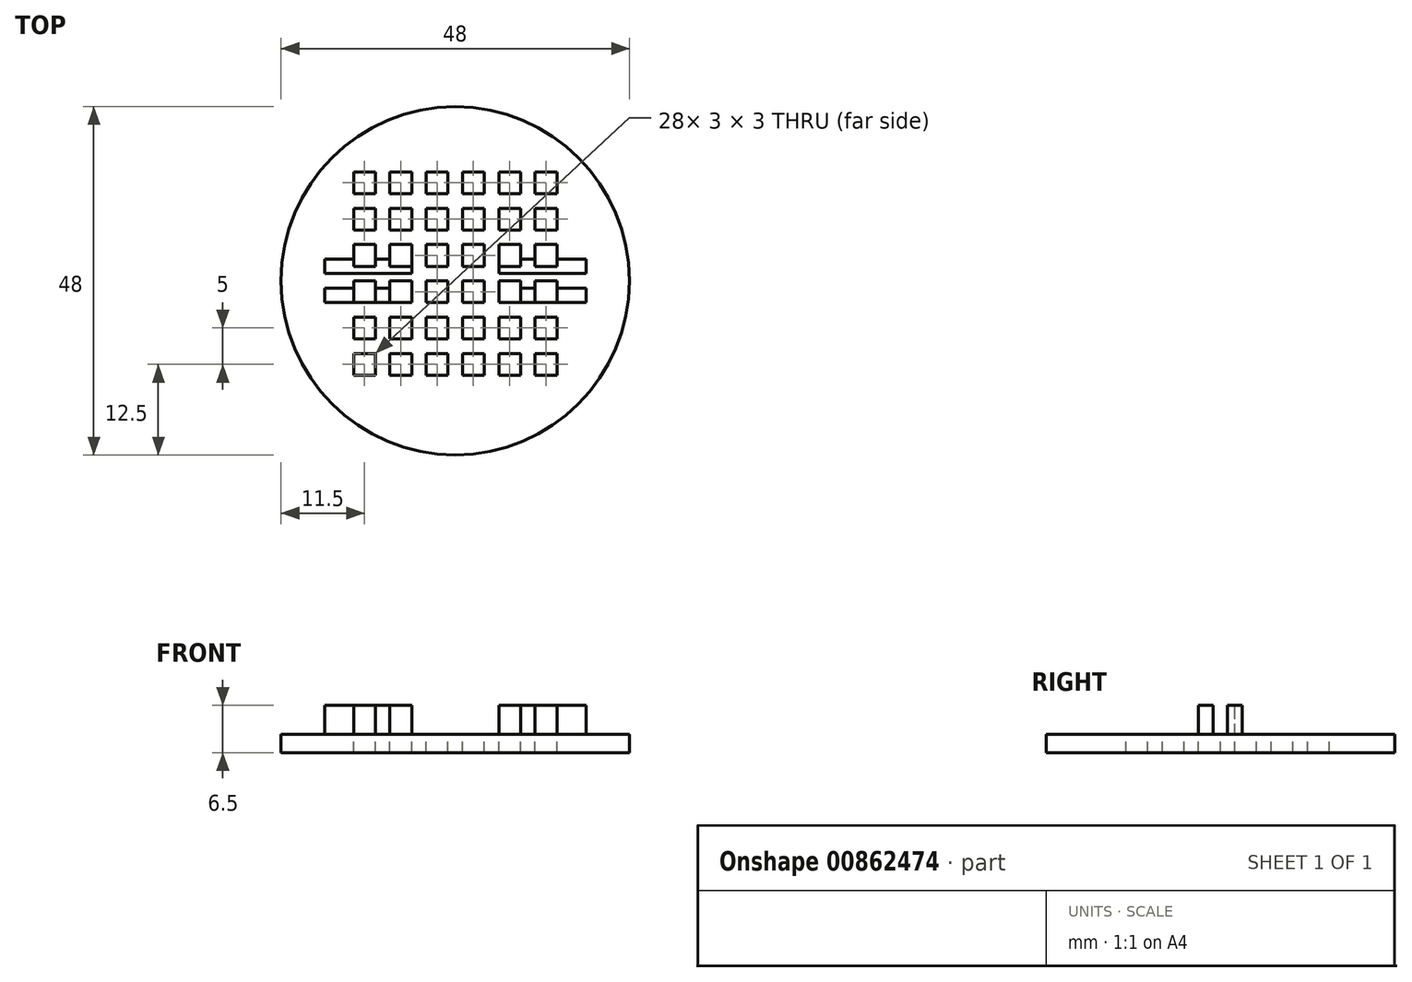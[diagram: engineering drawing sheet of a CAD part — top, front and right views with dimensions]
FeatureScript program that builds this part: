
annotation { "Feature Type Name" : "Feature", "Feature Type Description" : "" }
export const myFeature = defineFeature(function(context is Context, id is Id, definition is map)
    precondition{}
    {
        {
            var Q0;
            Q0=qCreatedBy(makeId("Top.planeOp"),FACE);
            var sketch = newSketch(context, id + "F0", { "sketchPlane" : qUnion([Q0])});
            skCircle(sketch, "E0", {"center": v(0, 0) * mm, "radius": 24 * mm});
            skSolve(sketch);
        }
        {
            var Q0;
            Q0 = qSketchRegion(id + "F0", true);
            extrude(context, id + "F1", {"entities" : qUnion([Q0]), "depth" : 2.5 * mm, "offsetDistance" : 25 * mm});
        }
        {
            var Q0;
            Q0=makeQuery(id+"F1.opExtrude","CAP_FACE",FACE,{"disambiguationData":[OSD([sQuery(id+"F0.wireOp",EDGE,"E0")])],"isStart":false});
            var sketch = newSketch(context, id + "F2", { "sketchPlane" : qUnion([Q0])});
            skCircle(sketch, "E1", {"center": v(-0.3, 0) * mm, "radius": 22 * mm});
            skSolve(sketch);
        }
        {
            var Q0;
            Q0=makeQuery(id+"F2.imprint","IMPRINT",FACE,{"disambiguationData":[TD([[makeQuery(id+"F2.imprint","IMPRINT",EDGE,{"derivedFrom":sQuery(id+"F2.wireOp",EDGE,"E1")}),1.0]])]});
            var sketch = newSketch(context, id + "F3", { "sketchPlane" : qUnion([Q0])});
            skLineSegment(sketch, "E2", {"start": v(-22.27, 1) * mm, "end": v(21.68, 1) * mm});
            skLineSegment(sketch, "E3", {"start": v(21.68, -1) * mm, "end": v(-22.27, -1) * mm});
            skLineSegment(sketch, "E4", {"start": v(6, -1) * mm, "end": v(6, 1) * mm});
            skLineSegment(sketch, "E5", {"start": v(-6, -1) * mm, "end": v(-6, 1) * mm});
            skSolve(sketch);
        }
        {
            var Q0;
            Q0=makeQuery(id+"F2.imprint","IMPRINT",FACE,{"disambiguationData":[TD([[makeQuery(id+"F2.imprint","IMPRINT",EDGE,{"derivedFrom":sQuery(id+"F2.wireOp",EDGE,"E1")}),1.0]])]});
            var sketch = newSketch(context, id + "F4", { "sketchPlane" : qUnion([Q0])});
            skLineSegment(sketch, "E6.bottom", {"start": v(18, -3) * mm, "end": v(6, -3) * mm});
            skLineSegment(sketch, "E6.top", {"start": v(18, -1) * mm, "end": v(6, -1) * mm});
            skLineSegment(sketch, "E6.left", {"start": v(18, -3) * mm, "end": v(18, -1) * mm});
            skLineSegment(sketch, "E6.right", {"start": v(6, -3) * mm, "end": v(6, -1) * mm});
            skLineSegment(sketch, "E7.bottom", {"start": v(6, 1) * mm, "end": v(18, 1) * mm});
            skLineSegment(sketch, "E7.top", {"start": v(6, 3) * mm, "end": v(18, 3) * mm});
            skLineSegment(sketch, "E7.left", {"start": v(6, 1) * mm, "end": v(6, 3) * mm});
            skLineSegment(sketch, "E7.right", {"start": v(18, 1) * mm, "end": v(18, 3) * mm});
            skLineSegment(sketch, "E8.bottom", {"start": v(-18, -1) * mm, "end": v(-6, -1) * mm});
            skLineSegment(sketch, "E8.top", {"start": v(-18, -3) * mm, "end": v(-6, -3) * mm});
            skLineSegment(sketch, "E8.left", {"start": v(-18, -1) * mm, "end": v(-18, -3) * mm});
            skLineSegment(sketch, "E8.right", {"start": v(-6, -1) * mm, "end": v(-6, -3) * mm});
            skLineSegment(sketch, "E9.bottom", {"start": v(-18, 1) * mm, "end": v(-6, 1) * mm});
            skLineSegment(sketch, "E9.top", {"start": v(-18, 3) * mm, "end": v(-6, 3) * mm});
            skLineSegment(sketch, "E9.left", {"start": v(-18, 1) * mm, "end": v(-18, 3) * mm});
            skLineSegment(sketch, "E9.right", {"start": v(-6, 1) * mm, "end": v(-6, 3) * mm});
            skSolve(sketch);
        }
        {
            var Q0;
            Q0 = qSketchRegion(id + "F4", true);
            extrude(context, id + "F5", {"entities" : qUnion([Q0]), "operationType" : NewBodyOperationType.ADD, "depth" : 4 * mm, "offsetDistance" : 25 * mm});
        }
        {
            var Q0;
            Q0=makeQuery(id+"F2.imprint","IMPRINT",FACE,{"disambiguationData":[TD([[makeQuery(id+"F2.imprint","IMPRINT",EDGE,{"derivedFrom":sQuery(id+"F2.wireOp",EDGE,"E1")}),1.0]])]});
            var sketch = newSketch(context, id + "F6", { "sketchPlane" : qUnion([Q0])});
            skLineSegment(sketch, "E10.bottom", {"start": v(11, -10) * mm, "end": v(14, -10) * mm});
            skLineSegment(sketch, "E10.top", {"start": v(11, -13) * mm, "end": v(14, -13) * mm});
            skLineSegment(sketch, "E10.left", {"start": v(11, -10) * mm, "end": v(11, -13) * mm});
            skLineSegment(sketch, "E10.right", {"start": v(14, -10) * mm, "end": v(14, -13) * mm});
            skLineSegment(sketch, "E11.0.1.0", {"start": v(11, -5) * mm, "end": v(14, -5) * mm});
            skLineSegment(sketch, "E11.0.1.1", {"start": v(11, -5) * mm, "end": v(11, -8) * mm});
            skLineSegment(sketch, "E11.0.1.2", {"start": v(11, -8) * mm, "end": v(14, -8) * mm});
            skLineSegment(sketch, "E11.0.1.3", {"start": v(14, -5) * mm, "end": v(14, -8) * mm});
            skLineSegment(sketch, "E11.0.2.0", {"start": v(11, 0) * mm, "end": v(14, 0) * mm});
            skLineSegment(sketch, "E11.0.2.1", {"start": v(11, 0) * mm, "end": v(11, -3) * mm});
            skLineSegment(sketch, "E11.0.2.2", {"start": v(11, -3) * mm, "end": v(14, -3) * mm});
            skLineSegment(sketch, "E11.0.2.3", {"start": v(14, 0) * mm, "end": v(14, -3) * mm});
            skLineSegment(sketch, "E11.0.3.0", {"start": v(11, 5) * mm, "end": v(14, 5) * mm});
            skLineSegment(sketch, "E11.0.3.1", {"start": v(11, 5) * mm, "end": v(11, 2) * mm});
            skLineSegment(sketch, "E11.0.3.2", {"start": v(11, 2) * mm, "end": v(14, 2) * mm});
            skLineSegment(sketch, "E11.0.3.3", {"start": v(14, 5) * mm, "end": v(14, 2) * mm});
            skLineSegment(sketch, "E11.0.4.0", {"start": v(11, 10) * mm, "end": v(14, 10) * mm});
            skLineSegment(sketch, "E11.0.4.1", {"start": v(11, 10) * mm, "end": v(11, 7) * mm});
            skLineSegment(sketch, "E11.0.4.2", {"start": v(11, 7) * mm, "end": v(14, 7) * mm});
            skLineSegment(sketch, "E11.0.4.3", {"start": v(14, 10) * mm, "end": v(14, 7) * mm});
            skLineSegment(sketch, "E11.0.5.0", {"start": v(11, 15) * mm, "end": v(14, 15) * mm});
            skLineSegment(sketch, "E11.0.5.1", {"start": v(11, 15) * mm, "end": v(11, 12) * mm});
            skLineSegment(sketch, "E11.0.5.2", {"start": v(11, 12) * mm, "end": v(14, 12) * mm});
            skLineSegment(sketch, "E11.0.5.3", {"start": v(14, 15) * mm, "end": v(14, 12) * mm});
            skLineSegment(sketch, "E11.1.0.0", {"start": v(6, -10) * mm, "end": v(9, -10) * mm});
            skLineSegment(sketch, "E11.1.0.1", {"start": v(6, -10) * mm, "end": v(6, -13) * mm});
            skLineSegment(sketch, "E11.1.0.2", {"start": v(6, -13) * mm, "end": v(9, -13) * mm});
            skLineSegment(sketch, "E11.1.0.3", {"start": v(9, -10) * mm, "end": v(9, -13) * mm});
            skLineSegment(sketch, "E11.1.1.0", {"start": v(6, -5) * mm, "end": v(9, -5) * mm});
            skLineSegment(sketch, "E11.1.1.1", {"start": v(6, -5) * mm, "end": v(6, -8) * mm});
            skLineSegment(sketch, "E11.1.1.2", {"start": v(6, -8) * mm, "end": v(9, -8) * mm});
            skLineSegment(sketch, "E11.1.1.3", {"start": v(9, -5) * mm, "end": v(9, -8) * mm});
            skLineSegment(sketch, "E11.1.2.0", {"start": v(6, 0) * mm, "end": v(9, 0) * mm});
            skLineSegment(sketch, "E11.1.2.1", {"start": v(6, 0) * mm, "end": v(6, -3) * mm});
            skLineSegment(sketch, "E11.1.2.2", {"start": v(6, -3) * mm, "end": v(9, -3) * mm});
            skLineSegment(sketch, "E11.1.2.3", {"start": v(9, 0) * mm, "end": v(9, -3) * mm});
            skLineSegment(sketch, "E11.1.3.0", {"start": v(6, 5) * mm, "end": v(9, 5) * mm});
            skLineSegment(sketch, "E11.1.3.1", {"start": v(6, 5) * mm, "end": v(6, 2) * mm});
            skLineSegment(sketch, "E11.1.3.2", {"start": v(6, 2) * mm, "end": v(9, 2) * mm});
            skLineSegment(sketch, "E11.1.3.3", {"start": v(9, 5) * mm, "end": v(9, 2) * mm});
            skLineSegment(sketch, "E11.1.4.0", {"start": v(6, 10) * mm, "end": v(9, 10) * mm});
            skLineSegment(sketch, "E11.1.4.1", {"start": v(6, 10) * mm, "end": v(6, 7) * mm});
            skLineSegment(sketch, "E11.1.4.2", {"start": v(6, 7) * mm, "end": v(9, 7) * mm});
            skLineSegment(sketch, "E11.1.4.3", {"start": v(9, 10) * mm, "end": v(9, 7) * mm});
            skLineSegment(sketch, "E11.1.5.0", {"start": v(6, 15) * mm, "end": v(9, 15) * mm});
            skLineSegment(sketch, "E11.1.5.1", {"start": v(6, 15) * mm, "end": v(6, 12) * mm});
            skLineSegment(sketch, "E11.1.5.2", {"start": v(6, 12) * mm, "end": v(9, 12) * mm});
            skLineSegment(sketch, "E11.1.5.3", {"start": v(9, 15) * mm, "end": v(9, 12) * mm});
            skLineSegment(sketch, "E11.2.0.0", {"start": v(1, -10) * mm, "end": v(4, -10) * mm});
            skLineSegment(sketch, "E11.2.0.1", {"start": v(1, -10) * mm, "end": v(1, -13) * mm});
            skLineSegment(sketch, "E11.2.0.2", {"start": v(1, -13) * mm, "end": v(4, -13) * mm});
            skLineSegment(sketch, "E11.2.0.3", {"start": v(4, -10) * mm, "end": v(4, -13) * mm});
            skLineSegment(sketch, "E11.2.1.0", {"start": v(1, -5) * mm, "end": v(4, -5) * mm});
            skLineSegment(sketch, "E11.2.1.1", {"start": v(1, -5) * mm, "end": v(1, -8) * mm});
            skLineSegment(sketch, "E11.2.1.2", {"start": v(1, -8) * mm, "end": v(4, -8) * mm});
            skLineSegment(sketch, "E11.2.1.3", {"start": v(4, -5) * mm, "end": v(4, -8) * mm});
            skLineSegment(sketch, "E11.2.2.0", {"start": v(1, 0) * mm, "end": v(4, 0) * mm});
            skLineSegment(sketch, "E11.2.2.1", {"start": v(1, 0) * mm, "end": v(1, -3) * mm});
            skLineSegment(sketch, "E11.2.2.2", {"start": v(1, -3) * mm, "end": v(4, -3) * mm});
            skLineSegment(sketch, "E11.2.2.3", {"start": v(4, 0) * mm, "end": v(4, -3) * mm});
            skLineSegment(sketch, "E11.2.3.0", {"start": v(1, 5) * mm, "end": v(4, 5) * mm});
            skLineSegment(sketch, "E11.2.3.1", {"start": v(1, 5) * mm, "end": v(1, 2) * mm});
            skLineSegment(sketch, "E11.2.3.2", {"start": v(1, 2) * mm, "end": v(4, 2) * mm});
            skLineSegment(sketch, "E11.2.3.3", {"start": v(4, 5) * mm, "end": v(4, 2) * mm});
            skLineSegment(sketch, "E11.2.4.0", {"start": v(1, 10) * mm, "end": v(4, 10) * mm});
            skLineSegment(sketch, "E11.2.4.1", {"start": v(1, 10) * mm, "end": v(1, 7) * mm});
            skLineSegment(sketch, "E11.2.4.2", {"start": v(1, 7) * mm, "end": v(4, 7) * mm});
            skLineSegment(sketch, "E11.2.4.3", {"start": v(4, 10) * mm, "end": v(4, 7) * mm});
            skLineSegment(sketch, "E11.2.5.0", {"start": v(1, 15) * mm, "end": v(4, 15) * mm});
            skLineSegment(sketch, "E11.2.5.1", {"start": v(1, 15) * mm, "end": v(1, 12) * mm});
            skLineSegment(sketch, "E11.2.5.2", {"start": v(1, 12) * mm, "end": v(4, 12) * mm});
            skLineSegment(sketch, "E11.2.5.3", {"start": v(4, 15) * mm, "end": v(4, 12) * mm});
            skLineSegment(sketch, "E11.3.0.0", {"start": v(-4, -10) * mm, "end": v(-1, -10) * mm});
            skLineSegment(sketch, "E11.3.0.1", {"start": v(-4, -10) * mm, "end": v(-4, -13) * mm});
            skLineSegment(sketch, "E11.3.0.2", {"start": v(-4, -13) * mm, "end": v(-1, -13) * mm});
            skLineSegment(sketch, "E11.3.0.3", {"start": v(-1, -10) * mm, "end": v(-1, -13) * mm});
            skLineSegment(sketch, "E11.3.1.0", {"start": v(-4, -5) * mm, "end": v(-1, -5) * mm});
            skLineSegment(sketch, "E11.3.1.1", {"start": v(-4, -5) * mm, "end": v(-4, -8) * mm});
            skLineSegment(sketch, "E11.3.1.2", {"start": v(-4, -8) * mm, "end": v(-1, -8) * mm});
            skLineSegment(sketch, "E11.3.1.3", {"start": v(-1, -5) * mm, "end": v(-1, -8) * mm});
            skLineSegment(sketch, "E11.3.2.0", {"start": v(-4, 0) * mm, "end": v(-1, 0) * mm});
            skLineSegment(sketch, "E11.3.2.1", {"start": v(-4, 0) * mm, "end": v(-4, -3) * mm});
            skLineSegment(sketch, "E11.3.2.2", {"start": v(-4, -3) * mm, "end": v(-1, -3) * mm});
            skLineSegment(sketch, "E11.3.2.3", {"start": v(-1, 0) * mm, "end": v(-1, -3) * mm});
            skLineSegment(sketch, "E11.3.3.0", {"start": v(-4, 5) * mm, "end": v(-1, 5) * mm});
            skLineSegment(sketch, "E11.3.3.1", {"start": v(-4, 5) * mm, "end": v(-4, 2) * mm});
            skLineSegment(sketch, "E11.3.3.2", {"start": v(-4, 2) * mm, "end": v(-1, 2) * mm});
            skLineSegment(sketch, "E11.3.3.3", {"start": v(-1, 5) * mm, "end": v(-1, 2) * mm});
            skLineSegment(sketch, "E11.3.4.0", {"start": v(-4, 10) * mm, "end": v(-1, 10) * mm});
            skLineSegment(sketch, "E11.3.4.1", {"start": v(-4, 10) * mm, "end": v(-4, 7) * mm});
            skLineSegment(sketch, "E11.3.4.2", {"start": v(-4, 7) * mm, "end": v(-1, 7) * mm});
            skLineSegment(sketch, "E11.3.4.3", {"start": v(-1, 10) * mm, "end": v(-1, 7) * mm});
            skLineSegment(sketch, "E11.3.5.0", {"start": v(-4, 15) * mm, "end": v(-1, 15) * mm});
            skLineSegment(sketch, "E11.3.5.1", {"start": v(-4, 15) * mm, "end": v(-4, 12) * mm});
            skLineSegment(sketch, "E11.3.5.2", {"start": v(-4, 12) * mm, "end": v(-1, 12) * mm});
            skLineSegment(sketch, "E11.3.5.3", {"start": v(-1, 15) * mm, "end": v(-1, 12) * mm});
            skLineSegment(sketch, "E11.4.0.0", {"start": v(-9, -10) * mm, "end": v(-6, -10) * mm});
            skLineSegment(sketch, "E11.4.0.1", {"start": v(-9, -10) * mm, "end": v(-9, -13) * mm});
            skLineSegment(sketch, "E11.4.0.2", {"start": v(-9, -13) * mm, "end": v(-6, -13) * mm});
            skLineSegment(sketch, "E11.4.0.3", {"start": v(-6, -10) * mm, "end": v(-6, -13) * mm});
            skLineSegment(sketch, "E11.4.1.0", {"start": v(-9, -5) * mm, "end": v(-6, -5) * mm});
            skLineSegment(sketch, "E11.4.1.1", {"start": v(-9, -5) * mm, "end": v(-9, -8) * mm});
            skLineSegment(sketch, "E11.4.1.2", {"start": v(-9, -8) * mm, "end": v(-6, -8) * mm});
            skLineSegment(sketch, "E11.4.1.3", {"start": v(-6, -5) * mm, "end": v(-6, -8) * mm});
            skLineSegment(sketch, "E11.4.2.0", {"start": v(-9, 0) * mm, "end": v(-6, 0) * mm});
            skLineSegment(sketch, "E11.4.2.1", {"start": v(-9, 0) * mm, "end": v(-9, -3) * mm});
            skLineSegment(sketch, "E11.4.2.2", {"start": v(-9, -3) * mm, "end": v(-6, -3) * mm});
            skLineSegment(sketch, "E11.4.2.3", {"start": v(-6, 0) * mm, "end": v(-6, -3) * mm});
            skLineSegment(sketch, "E11.4.3.0", {"start": v(-9, 5) * mm, "end": v(-6, 5) * mm});
            skLineSegment(sketch, "E11.4.3.1", {"start": v(-9, 5) * mm, "end": v(-9, 2) * mm});
            skLineSegment(sketch, "E11.4.3.2", {"start": v(-9, 2) * mm, "end": v(-6, 2) * mm});
            skLineSegment(sketch, "E11.4.3.3", {"start": v(-6, 5) * mm, "end": v(-6, 2) * mm});
            skLineSegment(sketch, "E11.4.4.0", {"start": v(-9, 10) * mm, "end": v(-6, 10) * mm});
            skLineSegment(sketch, "E11.4.4.1", {"start": v(-9, 10) * mm, "end": v(-9, 7) * mm});
            skLineSegment(sketch, "E11.4.4.2", {"start": v(-9, 7) * mm, "end": v(-6, 7) * mm});
            skLineSegment(sketch, "E11.4.4.3", {"start": v(-6, 10) * mm, "end": v(-6, 7) * mm});
            skLineSegment(sketch, "E11.4.5.0", {"start": v(-9, 15) * mm, "end": v(-6, 15) * mm});
            skLineSegment(sketch, "E11.4.5.1", {"start": v(-9, 15) * mm, "end": v(-9, 12) * mm});
            skLineSegment(sketch, "E11.4.5.2", {"start": v(-9, 12) * mm, "end": v(-6, 12) * mm});
            skLineSegment(sketch, "E11.4.5.3", {"start": v(-6, 15) * mm, "end": v(-6, 12) * mm});
            skLineSegment(sketch, "E11.5.0.0", {"start": v(-14, -10) * mm, "end": v(-11, -10) * mm});
            skLineSegment(sketch, "E11.5.0.1", {"start": v(-14, -10) * mm, "end": v(-14, -13) * mm});
            skLineSegment(sketch, "E11.5.0.2", {"start": v(-14, -13) * mm, "end": v(-11, -13) * mm});
            skLineSegment(sketch, "E11.5.0.3", {"start": v(-11, -10) * mm, "end": v(-11, -13) * mm});
            skLineSegment(sketch, "E11.5.1.0", {"start": v(-14, -5) * mm, "end": v(-11, -5) * mm});
            skLineSegment(sketch, "E11.5.1.1", {"start": v(-14, -5) * mm, "end": v(-14, -8) * mm});
            skLineSegment(sketch, "E11.5.1.2", {"start": v(-14, -8) * mm, "end": v(-11, -8) * mm});
            skLineSegment(sketch, "E11.5.1.3", {"start": v(-11, -5) * mm, "end": v(-11, -8) * mm});
            skLineSegment(sketch, "E11.5.2.0", {"start": v(-14, 0) * mm, "end": v(-11, 0) * mm});
            skLineSegment(sketch, "E11.5.2.1", {"start": v(-14, 0) * mm, "end": v(-14, -3) * mm});
            skLineSegment(sketch, "E11.5.2.2", {"start": v(-14, -3) * mm, "end": v(-11, -3) * mm});
            skLineSegment(sketch, "E11.5.2.3", {"start": v(-11, 0) * mm, "end": v(-11, -3) * mm});
            skLineSegment(sketch, "E11.5.3.0", {"start": v(-14, 5) * mm, "end": v(-11, 5) * mm});
            skLineSegment(sketch, "E11.5.3.1", {"start": v(-14, 5) * mm, "end": v(-14, 2) * mm});
            skLineSegment(sketch, "E11.5.3.2", {"start": v(-14, 2) * mm, "end": v(-11, 2) * mm});
            skLineSegment(sketch, "E11.5.3.3", {"start": v(-11, 5) * mm, "end": v(-11, 2) * mm});
            skLineSegment(sketch, "E11.5.4.0", {"start": v(-14, 10) * mm, "end": v(-11, 10) * mm});
            skLineSegment(sketch, "E11.5.4.1", {"start": v(-14, 10) * mm, "end": v(-14, 7) * mm});
            skLineSegment(sketch, "E11.5.4.2", {"start": v(-14, 7) * mm, "end": v(-11, 7) * mm});
            skLineSegment(sketch, "E11.5.4.3", {"start": v(-11, 10) * mm, "end": v(-11, 7) * mm});
            skLineSegment(sketch, "E11.5.5.0", {"start": v(-14, 15) * mm, "end": v(-11, 15) * mm});
            skLineSegment(sketch, "E11.5.5.1", {"start": v(-14, 15) * mm, "end": v(-14, 12) * mm});
            skLineSegment(sketch, "E11.5.5.2", {"start": v(-14, 12) * mm, "end": v(-11, 12) * mm});
            skLineSegment(sketch, "E11.5.5.3", {"start": v(-11, 15) * mm, "end": v(-11, 12) * mm});
            skLineSegment(sketch, "E11.direction1", {"start": v(11, -10) * mm, "end": v(6, -10) * mm, "construction": true});
            skLineSegment(sketch, "E11.direction2", {"start": v(11, -10) * mm, "end": v(11, -5) * mm, "construction": true});
            skSolve(sketch);
        }
        {
            var Q0;
            Q0 = qSketchRegion(id + "F6", true);
            extrude(context, id + "F7", {"entities" : qUnion([Q0]), "operationType" : NewBodyOperationType.REMOVE, "oppositeDirection" : true, "depth" : 2.5 * mm, "offsetDistance" : 25 * mm, "hasSecondDirection" : true, "secondDirectionOppositeDirection" : false, "secondDirectionDepth" : 25 * mm});
        }
    });
